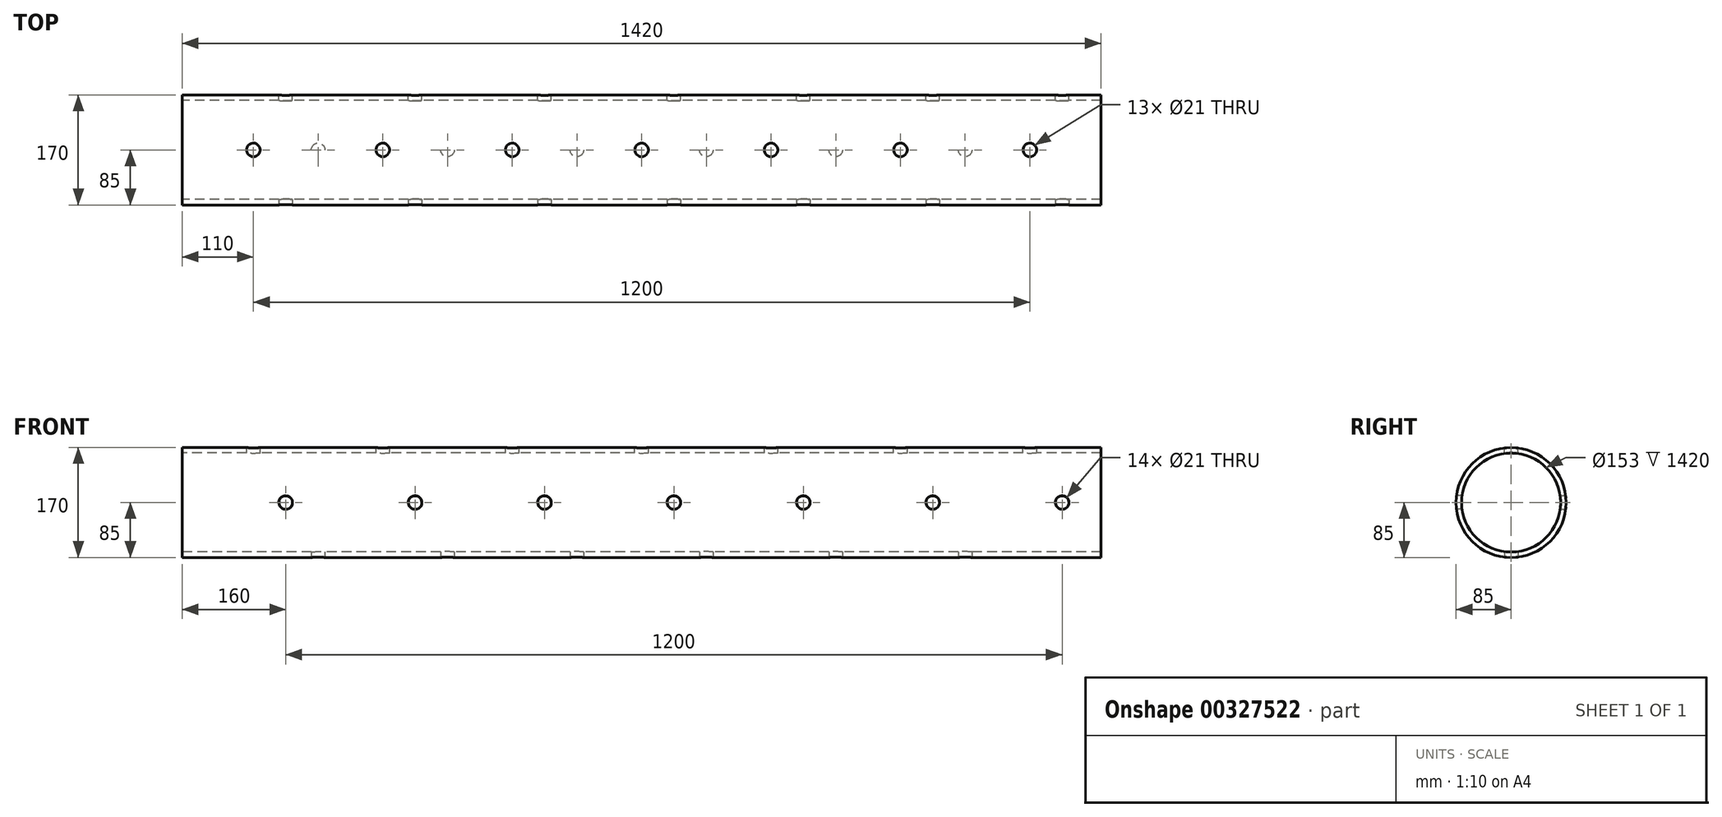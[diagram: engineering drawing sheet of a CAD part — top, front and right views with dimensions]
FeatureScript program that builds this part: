
annotation { "Feature Type Name" : "Feature", "Feature Type Description" : "" }
export const myFeature = defineFeature(function(context is Context, id is Id, definition is map)
    precondition{}
    {
        {
            var Q0;
            Q0=qCreatedBy(makeId("Right.planeOp"),FACE);
            var sketch = newSketch(context, id + "F0", { "sketchPlane" : qUnion([Q0])});
            skCircle(sketch, "E0", {"center": v(0, 0) * mm, "radius": 85 * mm});
            skCircle(sketch, "E1", {"center": v(0, 0) * mm, "radius": 76.5 * mm});
            skSolve(sketch);
        }
        {
            var Q0;
            Q0=makeQuery(id+"F0.imprint","IMPRINT",FACE,{"disambiguationData":[TD([[makeQuery(id+"F0.imprint","IMPRINT",EDGE,{"derivedFrom":sQuery(id+"F0.wireOp",EDGE,"E0")}),1.0]])]});
            extrude(context, id + "F1", {"entities" : qUnion([Q0]), "depth" : 1420 * mm});
        }
        {
            var Q0;
            Q0=qCreatedBy(makeId("Front.planeOp"),FACE);
            var sketch = newSketch(context, id + "F2", { "sketchPlane" : qUnion([Q0])});
            skLineSegment(sketch, "E2", {"start": v(0, 85) * mm, "end": v(1420, 85) * mm});
            skLineSegment(sketch, "E3", {"start": v(1420, -85) * mm, "end": v(0, -85) * mm});
            skLineSegment(sketch, "E4.0", {"start": v(0, 85) * mm, "end": v(0, -85) * mm});
            skLineSegment(sketch, "E5.0", {"start": v(1420, 85) * mm, "end": v(1420, -85) * mm});
            skLineSegment(sketch, "E6", {"start": v(0, 0) * mm, "end": v(160, 0) * mm});
            skLineSegment(sketch, "E7", {"start": v(160, 0) * mm, "end": v(360, 0) * mm});
            skLineSegment(sketch, "E8", {"start": v(360, 0) * mm, "end": v(560, 0) * mm});
            skLineSegment(sketch, "E9", {"start": v(560, 0) * mm, "end": v(760, 0) * mm});
            skLineSegment(sketch, "E10", {"start": v(760, 0) * mm, "end": v(960, 0) * mm});
            skLineSegment(sketch, "E11", {"start": v(960, 0) * mm, "end": v(1160, 0) * mm});
            skLineSegment(sketch, "E12", {"start": v(1160, 0) * mm, "end": v(1360, 0) * mm});
            skCircle(sketch, "E13", {"center": v(160, 0) * mm, "radius": 10.5 * mm});
            skCircle(sketch, "E14", {"center": v(360, 0) * mm, "radius": 10.5 * mm});
            skCircle(sketch, "E15", {"center": v(560, 0) * mm, "radius": 10.5 * mm});
            skCircle(sketch, "E16", {"center": v(760, 0) * mm, "radius": 10.5 * mm});
            skCircle(sketch, "E17", {"center": v(960, 0) * mm, "radius": 10.5 * mm});
            skCircle(sketch, "E18", {"center": v(1160, 0) * mm, "radius": 10.5 * mm});
            skCircle(sketch, "E19", {"center": v(1360, 0) * mm, "radius": 10.5 * mm});
            skSolve(sketch);
        }
        {
            var Q0;
            Q0=sQuery(id+"F2.wireOp",VERTEX,"E7.start");
            var Q1;
            Q1=sQuery(id+"F2.wireOp",VERTEX,"E8.start");
            var Q2;
            Q2=sQuery(id+"F2.wireOp",VERTEX,"E9.start");
            var Q3;
            Q3=sQuery(id+"F2.wireOp",VERTEX,"E16.center");
            var Q4;
            Q4=sQuery(id+"F2.wireOp",VERTEX,"E11.start");
            var Q5;
            Q5=sQuery(id+"F2.wireOp",VERTEX,"E12.end");
            var Q6;
            Q6=sQuery(id+"F2.wireOp",VERTEX,"E18.center");
            var Q7;
            Q7=makeQuery(id+"F1.opExtrude","SWEPT_BODY",BODY,{"disambiguationData":[OSD([sQuery(id+"F0.wireOp",EDGE,"E0"),sQuery(id+"F0.wireOp",EDGE,"E1")])]});
            hole(context, id + "F3", {"style" : HoleStyle.SIMPLE, "endStyle" : HoleEndStyle.BLIND, "holeDiameter" : 21 * mm, "holeDepth" : 1000 * mm, "tappedDepth" : 12 * mm, "tapClearance" : 3, "locations" : qUnion([Q0, Q1, Q2, Q3, Q4, Q5, Q6]), "scope" : qUnion([Q7]), "startStyle" : HoleStartStyle.PART});
        }
        {
            var Q0;
            Q0=qCreatedBy(makeId("Front.planeOp"),FACE);
            var sketch = newSketch(context, id + "F4", { "sketchPlane" : qUnion([Q0])});
            skLineSegment(sketch, "E20.0", {"start": v(0, 85) * mm, "end": v(0, -85) * mm});
            skLineSegment(sketch, "E21", {"start": v(0, 85) * mm, "end": v(1420, 85) * mm});
            skLineSegment(sketch, "E22", {"start": v(1420, -85) * mm, "end": v(0, -85) * mm});
            skLineSegment(sketch, "E23.0", {"start": v(1420, 85) * mm, "end": v(1420, -85) * mm});
            skLineSegment(sketch, "E24", {"start": v(0, 0) * mm, "end": v(160, 0) * mm});
            skLineSegment(sketch, "E25", {"start": v(160, 0) * mm, "end": v(360, 0) * mm});
            skLineSegment(sketch, "E26", {"start": v(360, 0) * mm, "end": v(560, 0) * mm});
            skLineSegment(sketch, "E27", {"start": v(560, 0) * mm, "end": v(760, 0) * mm});
            skLineSegment(sketch, "E28", {"start": v(760, 0) * mm, "end": v(960, 0) * mm});
            skLineSegment(sketch, "E29", {"start": v(960, 0) * mm, "end": v(1160, 0) * mm});
            skLineSegment(sketch, "E30", {"start": v(1160, 0) * mm, "end": v(1360, 0) * mm});
            skSolve(sketch);
        }
        {
            var Q0;
            Q0=sQuery(id+"F4.wireOp",VERTEX,"E25.start");
            var Q1;
            Q1=sQuery(id+"F4.wireOp",VERTEX,"E26.start");
            var Q2;
            Q2=sQuery(id+"F4.wireOp",VERTEX,"E27.start");
            var Q3;
            Q3=sQuery(id+"F4.wireOp",VERTEX,"E28.start");
            var Q4;
            Q4=sQuery(id+"F4.wireOp",VERTEX,"E28.end");
            var Q5;
            Q5=sQuery(id+"F4.wireOp",VERTEX,"E29.end");
            var Q6;
            Q6=sQuery(id+"F4.wireOp",VERTEX,"E30.end");
            var Q7;
            Q7=makeQuery(id+"F1.opExtrude","SWEPT_BODY",BODY,{"disambiguationData":[OSD([sQuery(id+"F0.wireOp",EDGE,"E0"),sQuery(id+"F0.wireOp",EDGE,"E1")])]});
            hole(context, id + "F5", {"style" : HoleStyle.SIMPLE, "endStyle" : HoleEndStyle.BLIND, "oppositeDirection" : true, "holeDiameter" : 21 * mm, "holeDepth" : 1000 * mm, "tappedDepth" : 12 * mm, "tapClearance" : 3, "locations" : qUnion([Q0, Q1, Q2, Q3, Q4, Q5, Q6]), "scope" : qUnion([Q7]), "startStyle" : HoleStartStyle.PART});
        }
        {
            var Q0;
            Q0=qCreatedBy(makeId("Top.planeOp"),FACE);
            var sketch = newSketch(context, id + "F6", { "sketchPlane" : qUnion([Q0])});
            skLineSegment(sketch, "E31", {"start": v(0, 85) * mm, "end": v(1420, 85) * mm});
            skLineSegment(sketch, "E32.0", {"start": v(0, 85) * mm, "end": v(0, -85) * mm});
            skLineSegment(sketch, "E33", {"start": v(1420, -85) * mm, "end": v(0, -85) * mm});
            skLineSegment(sketch, "E34.0", {"start": v(1420, 85) * mm, "end": v(1420, -85) * mm});
            skLineSegment(sketch, "E35", {"start": v(0, 0) * mm, "end": v(110, 0) * mm});
            skLineSegment(sketch, "E36", {"start": v(110, 0) * mm, "end": v(310, 0) * mm});
            skLineSegment(sketch, "E37", {"start": v(310, 0) * mm, "end": v(510, 0) * mm});
            skLineSegment(sketch, "E38", {"start": v(510, 0) * mm, "end": v(710, 0) * mm});
            skLineSegment(sketch, "E39", {"start": v(710, 0) * mm, "end": v(910, 0) * mm});
            skLineSegment(sketch, "E40", {"start": v(910, 0) * mm, "end": v(1110, 0) * mm});
            skLineSegment(sketch, "E41", {"start": v(1110, 0) * mm, "end": v(1310, 0) * mm});
            skLineSegment(sketch, "E42", {"start": v(0, 0) * mm, "end": v(-55.2, 0) * mm});
            skLineSegment(sketch, "E43", {"start": v(-55.2, 0) * mm, "end": v(1452.61, 0) * mm});
            skPoint(sketch, "E44", {"position": v(110, 0) * mm});
            skPoint(sketch, "E45", {"position": v(310, 0) * mm});
            skPoint(sketch, "E46", {"position": v(510, 0) * mm});
            skPoint(sketch, "E47", {"position": v(710, 0) * mm});
            skPoint(sketch, "E48", {"position": v(910, 0) * mm});
            skPoint(sketch, "E49", {"position": v(1110, 0) * mm});
            skPoint(sketch, "E50", {"position": v(1310, 0) * mm});
            skSolve(sketch);
        }
        {
            var Q0;
            Q0=sQuery(id+"F6.wireOp",VERTEX,"E46");
            var Q1;
            Q1=sQuery(id+"F6.wireOp",VERTEX,"E45");
            var Q2;
            Q2=sQuery(id+"F6.wireOp",VERTEX,"E44");
            var Q3;
            Q3=sQuery(id+"F6.wireOp",VERTEX,"E48");
            var Q4;
            Q4=sQuery(id+"F6.wireOp",VERTEX,"E47");
            var Q5;
            Q5=sQuery(id+"F6.wireOp",VERTEX,"E49");
            var Q6;
            Q6=sQuery(id+"F6.wireOp",VERTEX,"E50");
            var Q7;
            Q7=makeQuery(id+"F1.opExtrude","SWEPT_BODY",BODY,{"disambiguationData":[OSD([sQuery(id+"F0.wireOp",EDGE,"E0"),sQuery(id+"F0.wireOp",EDGE,"E1")])]});
            hole(context, id + "F7", {"style" : HoleStyle.SIMPLE, "endStyle" : HoleEndStyle.BLIND, "oppositeDirection" : true, "holeDiameter" : 21 * mm, "holeDepth" : 100 * mm, "tappedDepth" : 12 * mm, "tapClearance" : 3, "locations" : qUnion([Q0, Q1, Q2, Q3, Q4, Q5, Q6]), "scope" : qUnion([Q7]), "startStyle" : HoleStartStyle.PART});
        }
        {
            var Q0;
            Q0=qCreatedBy(makeId("Top.planeOp"),FACE);
            var sketch = newSketch(context, id + "F8", { "sketchPlane" : qUnion([Q0])});
            skLineSegment(sketch, "E51", {"start": v(0, 0) * mm, "end": v(210, 0) * mm});
            skLineSegment(sketch, "E52", {"start": v(210, 0) * mm, "end": v(410, 0) * mm});
            skLineSegment(sketch, "E53", {"start": v(410, 0) * mm, "end": v(610, 0) * mm});
            skLineSegment(sketch, "E54", {"start": v(610, 0) * mm, "end": v(810, 0) * mm});
            skLineSegment(sketch, "E55", {"start": v(810, 0) * mm, "end": v(1010, 0) * mm});
            skLineSegment(sketch, "E56", {"start": v(1010, 0) * mm, "end": v(1210, 0) * mm});
            skSolve(sketch);
        }
        {
            var Q0;
            Q0=sQuery(id+"F8.wireOp",VERTEX,"E51.end");
            var Q1;
            Q1=sQuery(id+"F8.wireOp",VERTEX,"E52.end");
            var Q2;
            Q2=sQuery(id+"F8.wireOp",VERTEX,"E53.end");
            var Q3;
            Q3=sQuery(id+"F8.wireOp",VERTEX,"E54.end");
            var Q4;
            Q4=sQuery(id+"F8.wireOp",VERTEX,"E55.end");
            var Q5;
            Q5=sQuery(id+"F8.wireOp",VERTEX,"E56.end");
            var Q6;
            Q6=makeQuery(id+"F1.opExtrude","SWEPT_BODY",BODY,{"disambiguationData":[OSD([sQuery(id+"F0.wireOp",EDGE,"E0"),sQuery(id+"F0.wireOp",EDGE,"E1")])]});
            hole(context, id + "F9", {"style" : HoleStyle.SIMPLE, "endStyle" : HoleEndStyle.BLIND, "holeDiameter" : 21 * mm, "holeDepth" : 100 * mm, "tappedDepth" : 12 * mm, "tapClearance" : 3, "locations" : qUnion([Q0, Q1, Q2, Q3, Q4, Q5]), "scope" : qUnion([Q6]), "startStyle" : HoleStartStyle.PART});
        }
    });
